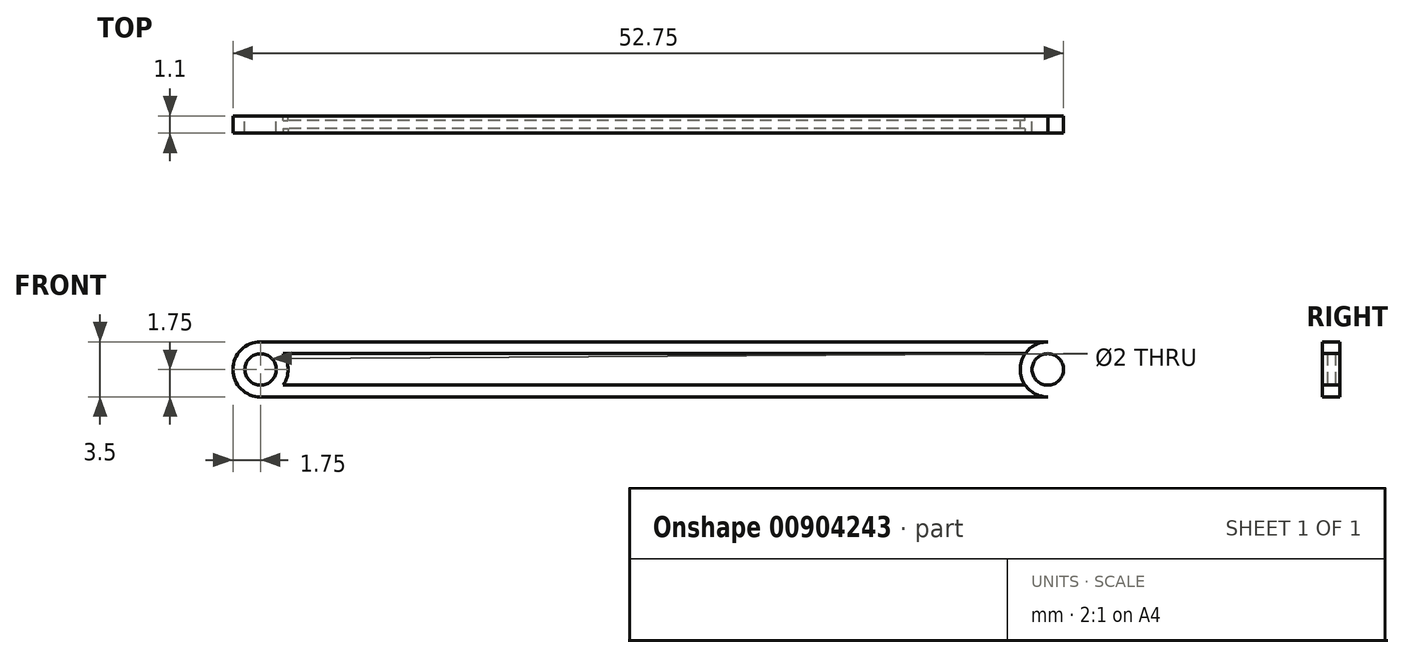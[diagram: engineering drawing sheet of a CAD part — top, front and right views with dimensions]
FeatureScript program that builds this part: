
annotation { "Feature Type Name" : "Feature", "Feature Type Description" : "" }
export const myFeature = defineFeature(function(context is Context, id is Id, definition is map)
    precondition{}
    {
        {
            var Q0;
            Q0=qCreatedBy(makeId("Front.planeOp"),FACE);
            var sketch = newSketch(context, id + "F0", { "sketchPlane" : qUnion([Q0])});
            skCircle(sketch, "E0", {"center": v(0, 0) * mm, "radius": 1 * mm});
            skCircle(sketch, "E1", {"center": v(0, 0) * mm, "radius": 1.75 * mm});
            skLineSegment(sketch, "E2", {"start": v(0, 0) * mm, "end": v(0, 1.75) * mm});
            skLineSegment(sketch, "E3", {"start": v(0, 1.75) * mm, "end": v(0, -1.75) * mm});
            skLineSegment(sketch, "E4", {"start": v(0, 1.75) * mm, "end": v(25, 1.75) * mm});
            skLineSegment(sketch, "E5.bottom", {"start": v(0, -1.75) * mm, "end": v(25, -1.75) * mm});
            skLineSegment(sketch, "E5.left", {"start": v(0, -1.75) * mm, "end": v(0, 1.75) * mm});
            skLineSegment(sketch, "E5.right", {"start": v(25, -1.75) * mm, "end": v(25, 1.75) * mm});
            skLineSegment(sketch, "E6.MirrorCS", {"start": v(50, 1.75) * mm, "end": v(25, 1.75) * mm});
            skLineSegment(sketch, "E7.MirrorCS", {"start": v(50, -1.75) * mm, "end": v(25, -1.75) * mm});
            skCircle(sketch, "E8.MirrorC", {"center": v(50, 0) * mm, "radius": 1.75 * mm});
            skCircle(sketch, "E9.MirrorC", {"center": v(50, 0) * mm, "radius": 1 * mm});
            skLineSegment(sketch, "E10.MirrorCS", {"start": v(50, -1.75) * mm, "end": v(50, 1.75) * mm});
            skLineSegment(sketch, "E11", {"start": v(50, 1) * mm, "end": v(0, 1) * mm});
            skLineSegment(sketch, "E12", {"start": v(50, -1) * mm, "end": v(0, -1) * mm});
            skSolve(sketch);
        }
        {
            var Q0;
            {var subQ1=sQuery(id+"F0.wireOp",EDGE,"E5.bottom");Q0=makeQuery(id+"F0.imprint","IMPRINT",FACE,{"disambiguationData":[TD([[makeQuery(id+"F0.imprint","IMPRINT",EDGE,{"derivedFrom":subQ1}),1.0]])]});}
            var Q1;
            Q1=makeQuery(id+"F0.imprint","IMPRINT",FACE,{"disambiguationData":[TD([[makeQuery(id+"F0.imprint","IMPRINT",EDGE,{"derivedFrom":sQuery(id+"F0.wireOp",EDGE,"E5.right")}),-1.0]])]});
            var Q2;
            {var subQ0=sQuery(id+"F0.wireOp",EDGE,"E10.MirrorCS");var subQ4=sQuery(id+"F0.wireOp",EDGE,"E9.MirrorC");var subQ6=makeQuery(id+"F0.imprint","INTERSECT",VERTEX,{"disambiguationData":[OD(0.0)],"derivedFrom":[subQ4,subQ0]});Q2=makeQuery(id+"F0.imprint","IMPRINT",FACE,{"disambiguationData":[TD([[makeQuery(id+"F0.imprint","IMPRINT",EDGE,{"disambiguationData":[TD([[subQ6,-1.0]])],"derivedFrom":subQ4}),1.0]])]});}
            var Q3;
            {var subQ0=sQuery(id+"F0.wireOp",EDGE,"E10.MirrorCS");var subQ4=sQuery(id+"F0.wireOp",EDGE,"E9.MirrorC");var subQ5=makeQuery(id+"F0.imprint","INTERSECT",VERTEX,{"disambiguationData":[OD(0.0)],"derivedFrom":[subQ4,subQ0]});Q3=makeQuery(id+"F0.imprint","IMPRINT",FACE,{"disambiguationData":[TD([[makeQuery(id+"F0.imprint","IMPRINT",EDGE,{"disambiguationData":[TD([[subQ5,1.0]])],"derivedFrom":subQ4}),1.0]])]});}
            var Q4;
            {var subQ0=sQuery(id+"F0.wireOp",EDGE,"E5.left");var subQ1=sQuery(id+"F0.wireOp",EDGE,"E0");var subQ2=makeQuery(id+"F0.imprint","INTERSECT",VERTEX,{"disambiguationData":[OD(0.0)],"derivedFrom":[subQ1,subQ0]});Q4=makeQuery(id+"F0.imprint","IMPRINT",FACE,{"disambiguationData":[TD([[makeQuery(id+"F0.imprint","IMPRINT",EDGE,{"disambiguationData":[TD([[subQ2,-1.0]])],"derivedFrom":subQ1}),-1.0]])]});}
            var Q5;
            {var subQ0=sQuery(id+"F0.wireOp",EDGE,"E5.left");var subQ1=sQuery(id+"F0.wireOp",EDGE,"E0");var subQ2=makeQuery(id+"F0.imprint","INTERSECT",VERTEX,{"disambiguationData":[OD(0.0)],"derivedFrom":[subQ1,subQ0]});Q5=makeQuery(id+"F0.imprint","IMPRINT",FACE,{"disambiguationData":[TD([[makeQuery(id+"F0.imprint","IMPRINT",EDGE,{"disambiguationData":[TD([[subQ2,1.0]])],"derivedFrom":subQ1}),-1.0]])]});}
            var Q6;
            {var subQ1=sQuery(id+"F0.wireOp",EDGE,"E8.MirrorC");var subQ3=sQuery(id+"F0.wireOp",EDGE,"E12");var subQ4=makeQuery(id+"F0.imprint","INTERSECT",VERTEX,{"derivedFrom":[subQ1,subQ3]});Q6=makeQuery(id+"F0.imprint","IMPRINT",FACE,{"disambiguationData":[TD([[makeQuery(id+"F0.imprint","IMPRINT",EDGE,{"disambiguationData":[TD([[subQ4,1.0]])],"derivedFrom":subQ1}),-1.0]])]});}
            var Q7;
            {var subQ1=sQuery(id+"F0.wireOp",EDGE,"E8.MirrorC");var subQ3=sQuery(id+"F0.wireOp",EDGE,"E11");var subQ4=makeQuery(id+"F0.imprint","INTERSECT",VERTEX,{"derivedFrom":[subQ1,subQ3]});Q7=makeQuery(id+"F0.imprint","IMPRINT",FACE,{"disambiguationData":[TD([[makeQuery(id+"F0.imprint","IMPRINT",EDGE,{"disambiguationData":[TD([[subQ4,-1.0]])],"derivedFrom":subQ1}),-1.0]])]});}
            var Q8;
            {var subQ0=sQuery(id+"F0.wireOp",EDGE,"E11");var subQ1=sQuery(id+"F0.wireOp",EDGE,"E1");var subQ2=makeQuery(id+"F0.imprint","INTERSECT",VERTEX,{"derivedFrom":[subQ1,subQ0]});Q8=makeQuery(id+"F0.imprint","IMPRINT",FACE,{"disambiguationData":[TD([[makeQuery(id+"F0.imprint","IMPRINT",EDGE,{"disambiguationData":[TD([[subQ2,1.0]])],"derivedFrom":subQ1}),-1.0]])]});}
            var Q9;
            {var subQ0=sQuery(id+"F0.wireOp",EDGE,"E4");Q9=makeQuery(id+"F0.imprint","IMPRINT",FACE,{"disambiguationData":[TD([[makeQuery(id+"F0.imprint","IMPRINT",EDGE,{"derivedFrom":subQ0}),-1.0]])]});}
            var Q10;
            {var subQ1=sQuery(id+"F0.wireOp",EDGE,"E1");var subQ3=sQuery(id+"F0.wireOp",EDGE,"E12");var subQ4=makeQuery(id+"F0.imprint","INTERSECT",VERTEX,{"derivedFrom":[subQ1,subQ3]});Q10=makeQuery(id+"F0.imprint","IMPRINT",FACE,{"disambiguationData":[TD([[makeQuery(id+"F0.imprint","IMPRINT",EDGE,{"disambiguationData":[TD([[subQ4,1.0]])],"derivedFrom":subQ1}),1.0]])]});}
            var Q11;
            {var subQ1=sQuery(id+"F0.wireOp",EDGE,"E1");var subQ3=sQuery(id+"F0.wireOp",EDGE,"E11");var subQ4=makeQuery(id+"F0.imprint","INTERSECT",VERTEX,{"derivedFrom":[subQ1,subQ3]});Q11=makeQuery(id+"F0.imprint","IMPRINT",FACE,{"disambiguationData":[TD([[makeQuery(id+"F0.imprint","IMPRINT",EDGE,{"disambiguationData":[TD([[subQ4,-1.0]])],"derivedFrom":subQ1}),1.0]])]});}
            extrude(context, id + "F1", {"entities" : qUnion([Q0, Q1, Q2, Q3, Q4, Q5, Q6, Q7, Q8, Q9, Q10, Q11]), "depth" : 1.1 * mm, "offsetDistance" : 25 * mm});
        }
        {
            var Q0;
            Q0=makeQuery(id+"F1.opExtrude","CAP_FACE",FACE,{"disambiguationData":[OSD([sQuery(id+"F0.wireOp",EDGE,"E0"),sQuery(id+"F0.wireOp",EDGE,"E1"),sQuery(id+"F0.wireOp",EDGE,"E5.bottom"),sQuery(id+"F0.wireOp",EDGE,"E4"),sQuery(id+"F0.wireOp",EDGE,"E6.MirrorCS"),sQuery(id+"F0.wireOp",EDGE,"E7.MirrorCS"),sQuery(id+"F0.wireOp",EDGE,"E8.MirrorC"),sQuery(id+"F0.wireOp",EDGE,"E9.MirrorC")])],"isStart":false});
            var sketch = newSketch(context, id + "F2", { "sketchPlane" : qUnion([Q0])});
            skLineSegment(sketch, "E13.0", {"start": v(50, 1) * mm, "end": v(0, 1) * mm});
            skLineSegment(sketch, "E14.0", {"start": v(50, -1) * mm, "end": v(0, -1) * mm});
            skCircle(sketch, "E15.0", {"center": v(0, 0) * mm, "radius": 1.75 * mm});
            skCircle(sketch, "E16.0", {"center": v(50, 0) * mm, "radius": 1.75 * mm});
            skSolve(sketch);
        }
        {
            var Q0;
            {var subQ0=sQuery(id+"F2.wireOp",EDGE,"E16.0");var subQ1=sQuery(id+"F2.wireOp",EDGE,"E13.0");var subQ2=makeQuery(id+"F2.imprint","INTERSECT",VERTEX,{"derivedFrom":[subQ1,subQ0]});Q0=makeQuery(id+"F2.imprint","IMPRINT",FACE,{"disambiguationData":[TD([[makeQuery(id+"F2.imprint","IMPRINT",EDGE,{"disambiguationData":[TD([[subQ2,-1.0]])],"derivedFrom":subQ1}),1.0]])]});}
            extrude(context, id + "F3", {"entities" : qUnion([Q0]), "operationType" : NewBodyOperationType.REMOVE, "oppositeDirection" : true, "depth" : 0.3 * mm, "offsetDistance" : 25 * mm});
        }
        {
            var Q0;
            {var subQ0=sQuery(id+"F0.wireOp",EDGE,"E12");var subQ1=sQuery(id+"F0.wireOp",EDGE,"E5.right");var subQ2=makeQuery(id+"F0.imprint","INTERSECT",VERTEX,{"derivedFrom":[subQ1,subQ0]});Q0=makeQuery(id+"F0.imprint","IMPRINT",FACE,{"disambiguationData":[TD([[makeQuery(id+"F0.imprint","IMPRINT",EDGE,{"disambiguationData":[TD([[subQ2,-1.0]])],"derivedFrom":subQ1}),-1.0]])]});}
            var Q1;
            {var subQ0=sQuery(id+"F0.wireOp",EDGE,"E11");var subQ1=sQuery(id+"F0.wireOp",EDGE,"E1");var subQ2=makeQuery(id+"F0.imprint","INTERSECT",VERTEX,{"derivedFrom":[subQ1,subQ0]});Q1=makeQuery(id+"F0.imprint","IMPRINT",FACE,{"disambiguationData":[TD([[makeQuery(id+"F0.imprint","IMPRINT",EDGE,{"disambiguationData":[TD([[subQ2,1.0]])],"derivedFrom":subQ1}),-1.0]])]});}
            extrude(context, id + "F4", {"entities" : qUnion([Q0, Q1]), "operationType" : NewBodyOperationType.REMOVE, "oppositeDirection" : true, "depth" : -0.3 * mm, "offsetDistance" : 25 * mm});
        }
    });
